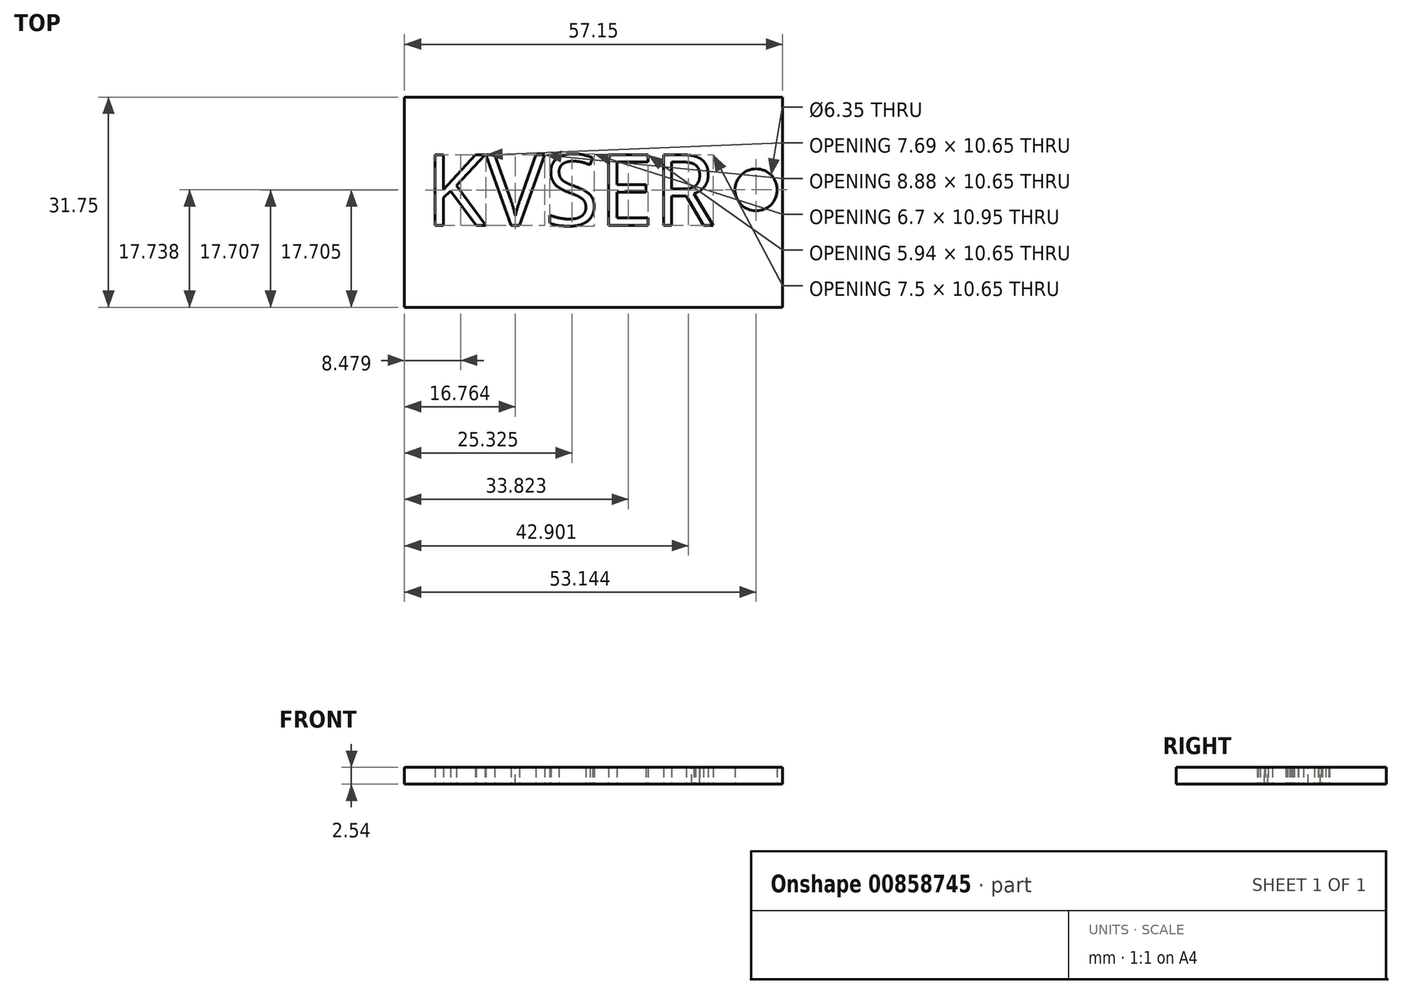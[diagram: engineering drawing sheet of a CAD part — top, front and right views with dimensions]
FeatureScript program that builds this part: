
annotation { "Feature Type Name" : "Feature", "Feature Type Description" : "" }
export const myFeature = defineFeature(function(context is Context, id is Id, definition is map)
    precondition{}
    {
        {
            var Q0;
            Q0=qCreatedBy(makeId("Top.planeOp"),FACE);
            var sketch = newSketch(context, id + "F0", { "sketchPlane" : qUnion([Q0])});
            skLineSegment(sketch, "E0.bottom", {"start": v(-58.67, 30.59) * mm, "end": v(-1.52, 30.59) * mm});
            skLineSegment(sketch, "E0.top", {"start": v(-58.67, -1.16) * mm, "end": v(-1.52, -1.16) * mm});
            skLineSegment(sketch, "E0.left", {"start": v(-58.67, 30.59) * mm, "end": v(-58.67, -1.16) * mm});
            skLineSegment(sketch, "E0.right", {"start": v(-1.52, 30.59) * mm, "end": v(-1.52, -1.16) * mm});
            skText(sketch, "E1", { "text": "KVSER\n", "fontName": "OpenSans-Regular.ttf"});
            skCircle(sketch, "E2", {"center": v(-5.53, 16.58) * mm, "radius": 3.18 * mm});
            skLineSegment(sketch, "E3", {"start": v(-18.38, 19.48) * mm, "end": v(-19.7, 19.48) * mm});
            skLineSegment(sketch, "E4", {"start": v(-18.23, 18.36) * mm, "end": v(-19.64, 18.36) * mm});
            skLineSegment(sketch, "E5", {"start": v(-15.27, 20.55) * mm, "end": v(-14.4, 21.47) * mm});
            skLineSegment(sketch, "E6", {"start": v(-14.15, 19.97) * mm, "end": v(-13.28, 20.7) * mm});
            skLineSegment(sketch, "E7", {"start": v(-14.74, 17.2) * mm, "end": v(-13.38, 16.6) * mm});
            skPoint(sketch, "E7.endSnap0", {"position": v(-11.04, 16.6) * mm});
            skLineSegment(sketch, "E8", {"start": v(-14.1, 18.07) * mm, "end": v(-12.94, 18.07) * mm});
            skLineSegment(sketch, "E9", {"start": v(-12.94, 18.07) * mm, "end": v(-12.64, 18.07) * mm});
            skLineSegment(sketch, "E10", {"start": v(-18.38, 19.48) * mm, "end": v(-17.65, 19.48) * mm});
            skLineSegment(sketch, "E11", {"start": v(-14.15, 19.97) * mm, "end": v(-14.43, 19.84) * mm});
            skLineSegment(sketch, "E12", {"start": v(-14.4, 21.47) * mm, "end": v(-14.28, 21.6) * mm});
            skLineSegment(sketch, "E13", {"start": v(-14.1, 18.07) * mm, "end": v(-14.46, 18.07) * mm});
            const initialGuessF0  = {"E1": [-0.0555, 0.01122, 1, 0, 0.01074]};
            skSetInitialGuess(sketch, initialGuessF0);
            skSolve(sketch);
        }
        {
            var Q0;
            Q0=makeQuery(id+"F0.imprint","IMPRINT",FACE,{"disambiguationData":[TD([[makeQuery(id+"F0.imprint","IMPRINT",EDGE,{"derivedFrom":sQuery(id+"F0.wireOp",EDGE,"E1.sketch_text.stroke-69")}),1.0]])]});
            var Q1;
            Q1=makeQuery(id+"F0.imprint","IMPRINT",FACE,{"disambiguationData":[TD([[makeQuery(id+"F0.imprint","IMPRINT",EDGE,{"derivedFrom":sQuery(id+"F0.wireOp",EDGE,"E0.bottom")}),-1.0]])]});
            extrude(context, id + "F1", {"entities" : qUnion([Q0, Q1]), "depth" : 2.54 * mm, "offsetDistance" : 25.4 * mm});
        }
    });
